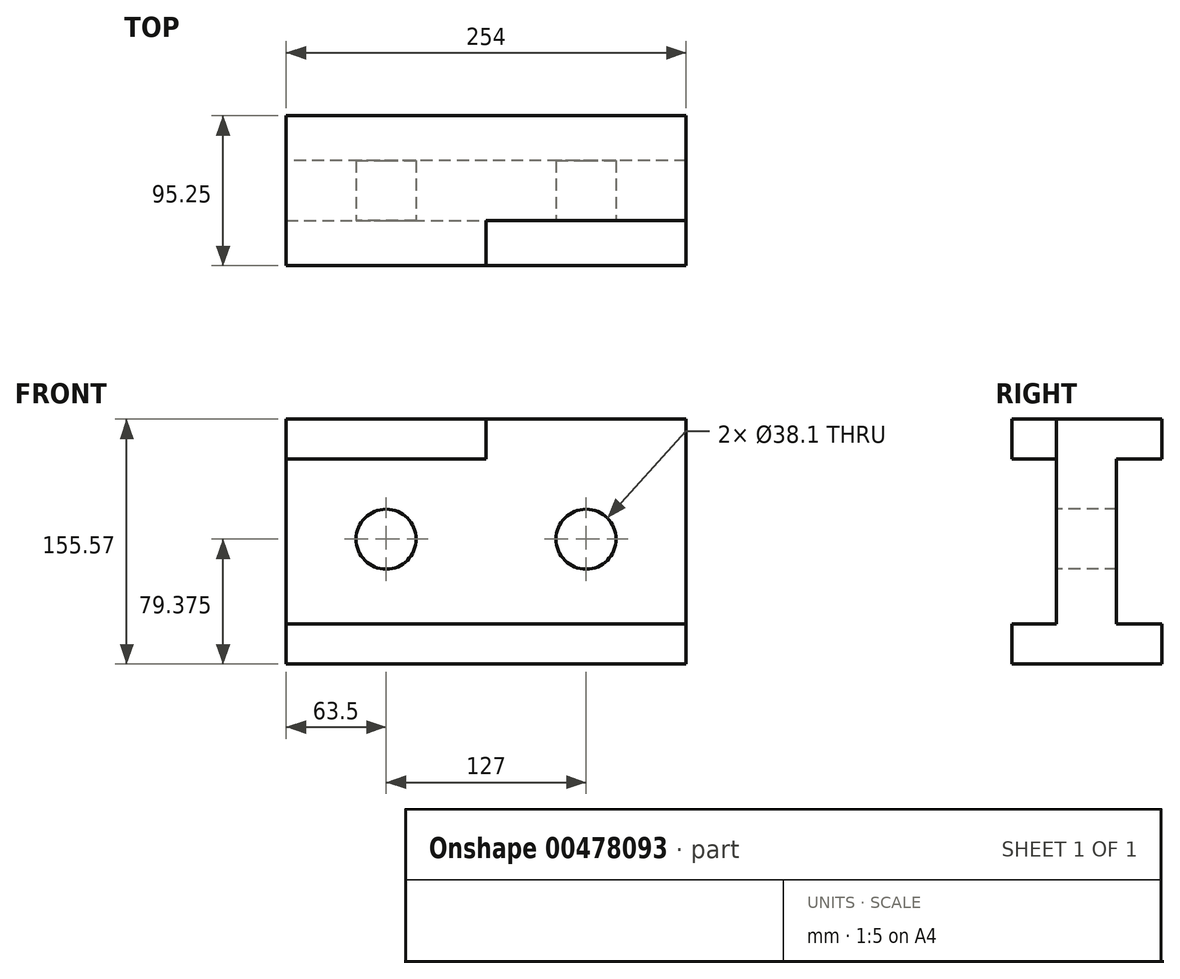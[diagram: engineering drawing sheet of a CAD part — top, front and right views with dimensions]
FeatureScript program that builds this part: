
annotation { "Feature Type Name" : "Feature", "Feature Type Description" : "" }
export const myFeature = defineFeature(function(context is Context, id is Id, definition is map)
    precondition{}
    {
        {
            var Q0;
            Q0=qCreatedBy(makeId("Right.planeOp"),FACE);
            var sketch = newSketch(context, id + "F0", { "sketchPlane" : qUnion([Q0])});
            skLineSegment(sketch, "E0", {"start": v(0, 0) * mm, "end": v(0, 155.58) * mm, "construction": true});
            skLineSegment(sketch, "E1", {"start": v(0, 0) * mm, "end": v(95.25, 0) * mm});
            skLineSegment(sketch, "E2", {"start": v(95.25, 0) * mm, "end": v(95.25, 25.4) * mm});
            skLineSegment(sketch, "E3", {"start": v(95.25, 25.4) * mm, "end": v(66.67, 25.4) * mm});
            skLineSegment(sketch, "E4", {"start": v(66.67, 25.4) * mm, "end": v(66.67, 130.18) * mm});
            skLineSegment(sketch, "E5", {"start": v(66.67, 130.18) * mm, "end": v(95.25, 130.18) * mm});
            skLineSegment(sketch, "E6", {"start": v(95.25, 130.18) * mm, "end": v(95.25, 155.58) * mm});
            skLineSegment(sketch, "E7", {"start": v(95.25, 155.58) * mm, "end": v(28.57, 155.58) * mm});
            skLineSegment(sketch, "E8", {"start": v(28.57, 155.58) * mm, "end": v(28.57, 25.4) * mm});
            skLineSegment(sketch, "E9", {"start": v(28.57, 25.4) * mm, "end": v(0, 25.4) * mm});
            skLineSegment(sketch, "E10", {"start": v(0, 25.4) * mm, "end": v(0, 0) * mm});
            skSolve(sketch);
        }
        {
            var Q0;
            Q0=makeQuery(id+"F0.imprint","IMPRINT",FACE,{"disambiguationData":[TD([[makeQuery(id+"F0.imprint","IMPRINT",EDGE,{"derivedFrom":sQuery(id+"F0.wireOp",EDGE,"E1")}),1.0]])]});
            extrude(context, id + "F1", {"entities" : qUnion([Q0]), "depth" : 254 * mm});
        }
        {
            var Q0;
            Q0=makeQuery(id+"F1.opExtrude","SWEPT_FACE",FACE,{"disambiguationData":[OSD([sQuery(id+"F0.wireOp",EDGE,"E8")])]});
            var sketch = newSketch(context, id + "F2", { "sketchPlane" : qUnion([Q0])});
            skLineSegment(sketch, "E11", {"start": v(254, 25.4) * mm, "end": v(254, 79.38) * mm, "construction": true});
            skLineSegment(sketch, "E12", {"start": v(254, 79.38) * mm, "end": v(190.5, 79.38) * mm, "construction": true});
            skLineSegment(sketch, "E13", {"start": v(190.5, 79.38) * mm, "end": v(63.5, 79.37) * mm, "construction": true});
            skLineSegment(sketch, "E14", {"start": v(63.5, 79.37) * mm, "end": v(0, 79.37) * mm, "construction": true});
            skLineSegment(sketch, "E15", {"start": v(0, 155.58) * mm, "end": v(0, 130.17) * mm});
            skLineSegment(sketch, "E16", {"start": v(0, 130.17) * mm, "end": v(127, 130.17) * mm});
            skLineSegment(sketch, "E17", {"start": v(127, 130.17) * mm, "end": v(127, 155.58) * mm});
            skCircle(sketch, "E18", {"center": v(63.5, 79.37) * mm, "radius": 19.05 * mm});
            skCircle(sketch, "E19", {"center": v(190.5, 79.38) * mm, "radius": 19.05 * mm});
            skSolve(sketch);
        }
        {
            var Q0;
            Q0=makeQuery(id+"F2.imprint","IMPRINT",FACE,{"disambiguationData":[TD([[makeQuery(id+"F2.imprint","IMPRINT",EDGE,{"derivedFrom":sQuery(id+"F2.wireOp",EDGE,"E18")}),1.0]])]});
            var Q1;
            Q1=makeQuery(id+"F2.imprint","IMPRINT",FACE,{"disambiguationData":[TD([[makeQuery(id+"F2.imprint","IMPRINT",EDGE,{"derivedFrom":sQuery(id+"F2.wireOp",EDGE,"E19")}),1.0]])]});
            extrude(context, id + "F3", {"entities" : qUnion([Q0, Q1]), "operationType" : NewBodyOperationType.REMOVE, "oppositeDirection" : true, "depth" : 101.35 * mm});
        }
        {
            var Q0;
            {var subQ0=sQuery(id+"F2.wireOp",EDGE,"E15");Q0=makeQuery(id+"F2.imprint","IMPRINT",FACE,{"disambiguationData":[TD([[makeQuery(id+"F2.imprint","IMPRINT",EDGE,{"derivedFrom":subQ0}),1.0]])]});}
            var Q1;
            Q1=makeQuery(id+"F1.opExtrude","SWEPT_FACE",FACE,{"disambiguationData":[OSD([sQuery(id+"F0.wireOp",EDGE,"E10")])]});
            extrude(context, id + "F4", {"entities" : qUnion([Q0]), "operationType" : NewBodyOperationType.ADD, "endBound" : BoundingType.UP_TO_SURFACE, "endBoundEntityFace" : qUnion([Q1]), "depth" : 25.4 * mm});
        }
    });
